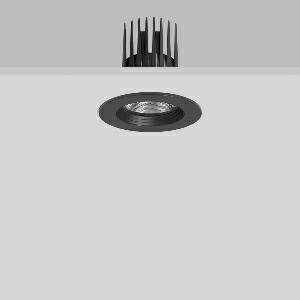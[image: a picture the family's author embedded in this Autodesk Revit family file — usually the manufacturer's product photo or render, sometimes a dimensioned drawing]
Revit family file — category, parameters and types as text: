
# Revit family: heledon_mini_e_901742_003_3_76_4941
name_source: partatom
category: Lighting Fixtures
units: mm (PartAtom-declared; Revit-internal decimal feet)

## family parameters
Cut with Voids When Loaded = No
Host = Face
Light Source = No
Part Type = Normal
Room Calculation Point = No
Round Connector Dimension = Use Diameter
Shared = No

## types (1)
- HELEDON mini E (1 x LED Modul 935, 2650 lm, 3500)
    Apparent Load = 20 VA
    Approval mark = CE
    CIE Flux Codes = 95 99 100 100 100
    Color Rendering = 92
    Color Temperature = 3500
    Default Elevation = 1800 mm
    Description = Series: HELEDON mini
Round recessed downlight. Housing: die-cast aluminium, powder-coated. Black plastic ring and recessed LED to prevent glare from the side. Optical assembly with reflector made of MIRO-Silver with 98% total light reflection for outstanding efficiency - can be changed without tools. Best colour rendering index Ra>90. Suitable for Recessed ceiling mounting. Installation without tools thanks to spring fastening system. Including separate LED converter with connecting cable 600 mm.High quality converter without flickering and stroboscopic effect. Through-wiring box (5 pole) available as accessory. The following accessories can be mounted without use of tools: interchangeable lenses, decorative glasses, honeycomb louvre, clear and frosted diffusers, white interchangeable plastic ring. 
Colour: deep black, matt (RAL 9005)
Diameter: 124 mm
Height: 3 mm
Cut-out diameter: 114 mm
Recess height: 170 mm
Luminaire: recess height: 120 mm
Lamp: LED
Socket: without socket
Colour temperature: 3500K
Colour rendering index (CRI): 92
System power: 20 W
Rated luminous flux: 2650 lm
Luminous efficiency: 133 lm/W
Control gear: Converter, dimmable, DALI
Protection class: II
Type of protection: IP 20
    Height = 0 mm  [stored 0 ft]
    Lamp = 1 x LED Modul 935
    Lamp Light Flux = 2650 lm
    Lamp count = 1
    Length = 124 mm  [stored 0.406824 ft]
    Lifetime = 50000 h
    Luminous efficacy = 133 lm/W
    Manufacturer = RZB
    ModVariant = No
    Model = 901742.003.3.76
    Mounting Place = Ceiling
    Mounting Type = Recessed
    Number of Poles = 1
    OnlyDefault = Yes
    Power Factor = 1
    Product Name = HELEDON mini E
    Product group = Recessed downlights
    ProductGroupID = 402
    Protection Class = Protection class II
    Protection Degree = IP 20
    RLX_Detail_Level = 1
    RLX_Emergency_Light_Flux = 0 lm
    RLX_Emergency_Type = 0
    RLX_Emergency_Type_DB = No
    RlxData = <blob elided: 128949 chars, md5=6a438323>
    Socket = socket
    Standby Power = 0 W
    System Light Flux = 2650 lm
    System Power = 20 W
    Type Comments = Product without accessories
    Type Image = 901657.003.jpg
    URL = http://relux.com
    VarID = ---
    Voltage = 230 V
    Voltage Range = 220-240 V
    Weight = 0.00 kg
    Width = 0 mm  [stored 0 ft]

note: [stored X ft] marks values corroborated as IEEE doubles in the binary element streams (Revit-internal decimal feet)

## geometry (parser evidence)
native form markers: Blend x4, Sweep x10
no freeform markers — native parametric forms only
